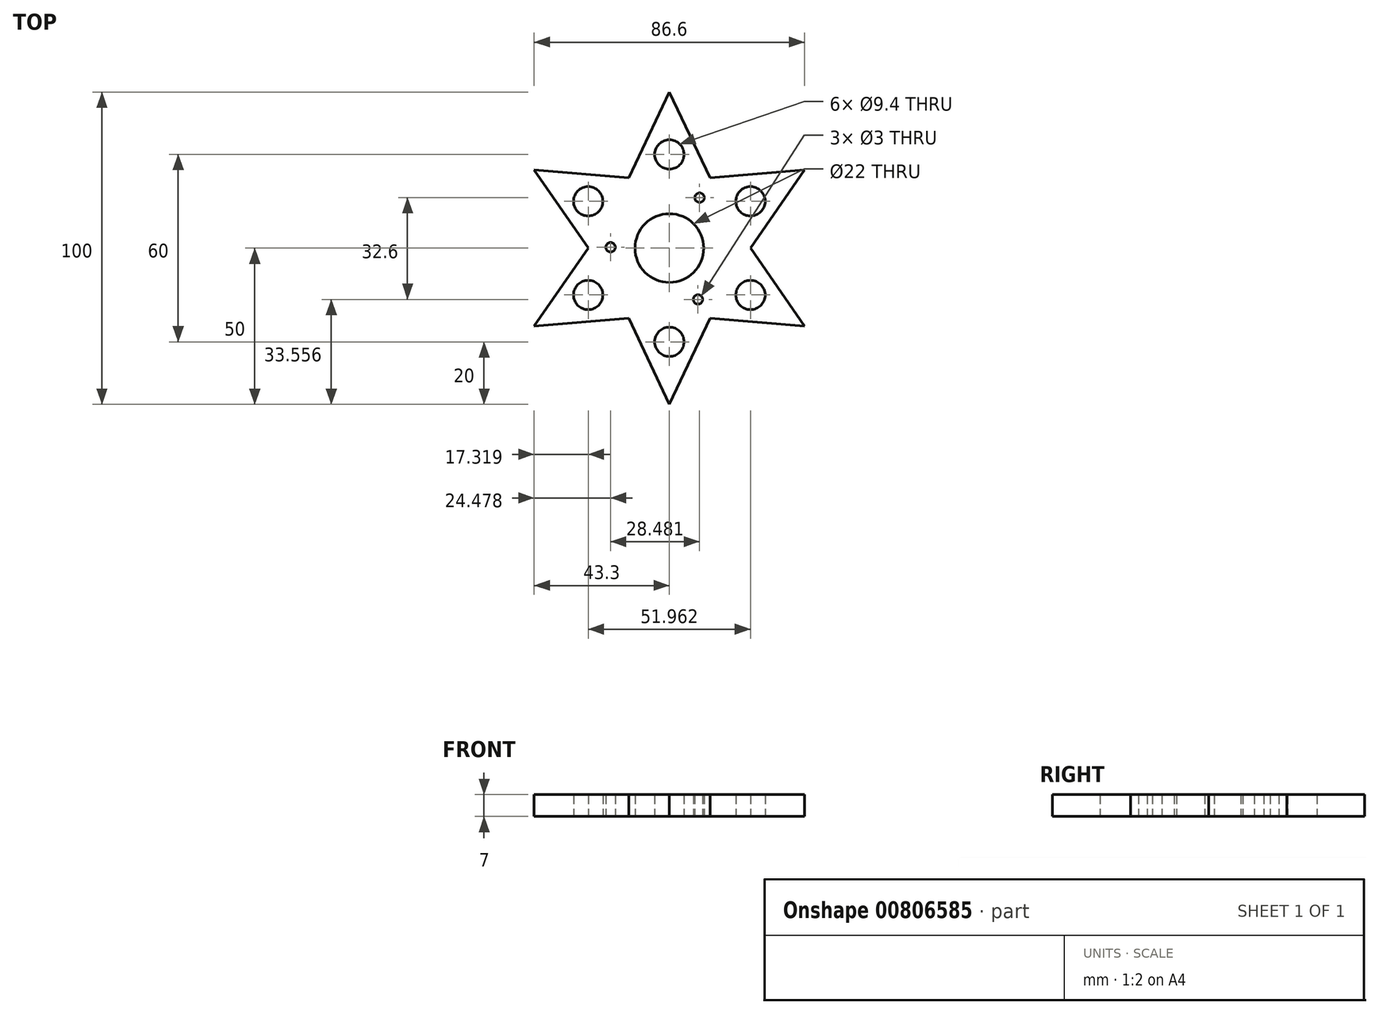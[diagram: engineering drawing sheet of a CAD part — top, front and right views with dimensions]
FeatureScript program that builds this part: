
annotation { "Feature Type Name" : "Feature", "Feature Type Description" : "" }
export const myFeature = defineFeature(function(context is Context, id is Id, definition is map)
    precondition{}
    {
        {
            var Q0;
            Q0=qCreatedBy(makeId("Top.planeOp"),FACE);
            var sketch = newSketch(context, id + "F0", { "sketchPlane" : qUnion([Q0])});
            skCircle(sketch, "E0", {"center": v(0, 0) * mm, "radius": 11 * mm});
            skLineSegment(sketch, "E1", {"start": v(-13, 22.5) * mm, "end": v(0, 50) * mm});
            skLineSegment(sketch, "E2.MirrorCS", {"start": v(13, 22.5) * mm, "end": v(0, 50) * mm});
            skLineSegment(sketch, "E3.1.0", {"start": v(-13, 22.5) * mm, "end": v(-43.3, 25) * mm});
            skLineSegment(sketch, "E3.1.1", {"start": v(-25.98, 0) * mm, "end": v(-43.3, 25) * mm});
            skLineSegment(sketch, "E3.2.0", {"start": v(-25.98, 0) * mm, "end": v(-43.3, -25) * mm});
            skLineSegment(sketch, "E3.2.1", {"start": v(-13, -22.5) * mm, "end": v(-43.3, -25) * mm});
            skLineSegment(sketch, "E3.3.0", {"start": v(-13, -22.5) * mm, "end": v(0, -50) * mm});
            skLineSegment(sketch, "E3.3.1", {"start": v(13, -22.5) * mm, "end": v(0, -50) * mm});
            skLineSegment(sketch, "E3.4.0", {"start": v(13, -22.5) * mm, "end": v(43.3, -25) * mm});
            skLineSegment(sketch, "E3.4.1", {"start": v(25.98, 0) * mm, "end": v(43.3, -25) * mm});
            skLineSegment(sketch, "E3.5.0", {"start": v(25.98, 0) * mm, "end": v(43.3, 25) * mm});
            skLineSegment(sketch, "E3.5.1", {"start": v(13, 22.5) * mm, "end": v(43.3, 25) * mm});
            skCircle(sketch, "E4", {"center": v(25.98, 15) * mm, "radius": 4.7 * mm});
            skCircle(sketch, "E5.1.0", {"center": v(0, 30) * mm, "radius": 4.7 * mm});
            skCircle(sketch, "E5.2.0", {"center": v(-25.98, 15) * mm, "radius": 4.7 * mm});
            skCircle(sketch, "E5.3.0", {"center": v(-25.98, -15) * mm, "radius": 4.7 * mm});
            skCircle(sketch, "E5.4.0", {"center": v(0, -30) * mm, "radius": 4.7 * mm});
            skCircle(sketch, "E5.5.0", {"center": v(25.98, -15) * mm, "radius": 4.7 * mm});
            skCircle(sketch, "E6", {"center": v(9.66, 16.16) * mm, "radius": 1.5 * mm});
            skCircle(sketch, "E7.1.0", {"center": v(-18.82, 0.29) * mm, "radius": 1.5 * mm});
            skCircle(sketch, "E7.2.0", {"center": v(9.16, -16.44) * mm, "radius": 1.5 * mm});
            skSolve(sketch);
        }
        {
            var Q0;
            Q0 = qSketchRegion(id + "F0", true);
            extrude(context, id + "F1", {"entities" : qUnion([Q0]), "depth" : 7 * mm, "offsetDistance" : 25 * mm});
        }
    });
